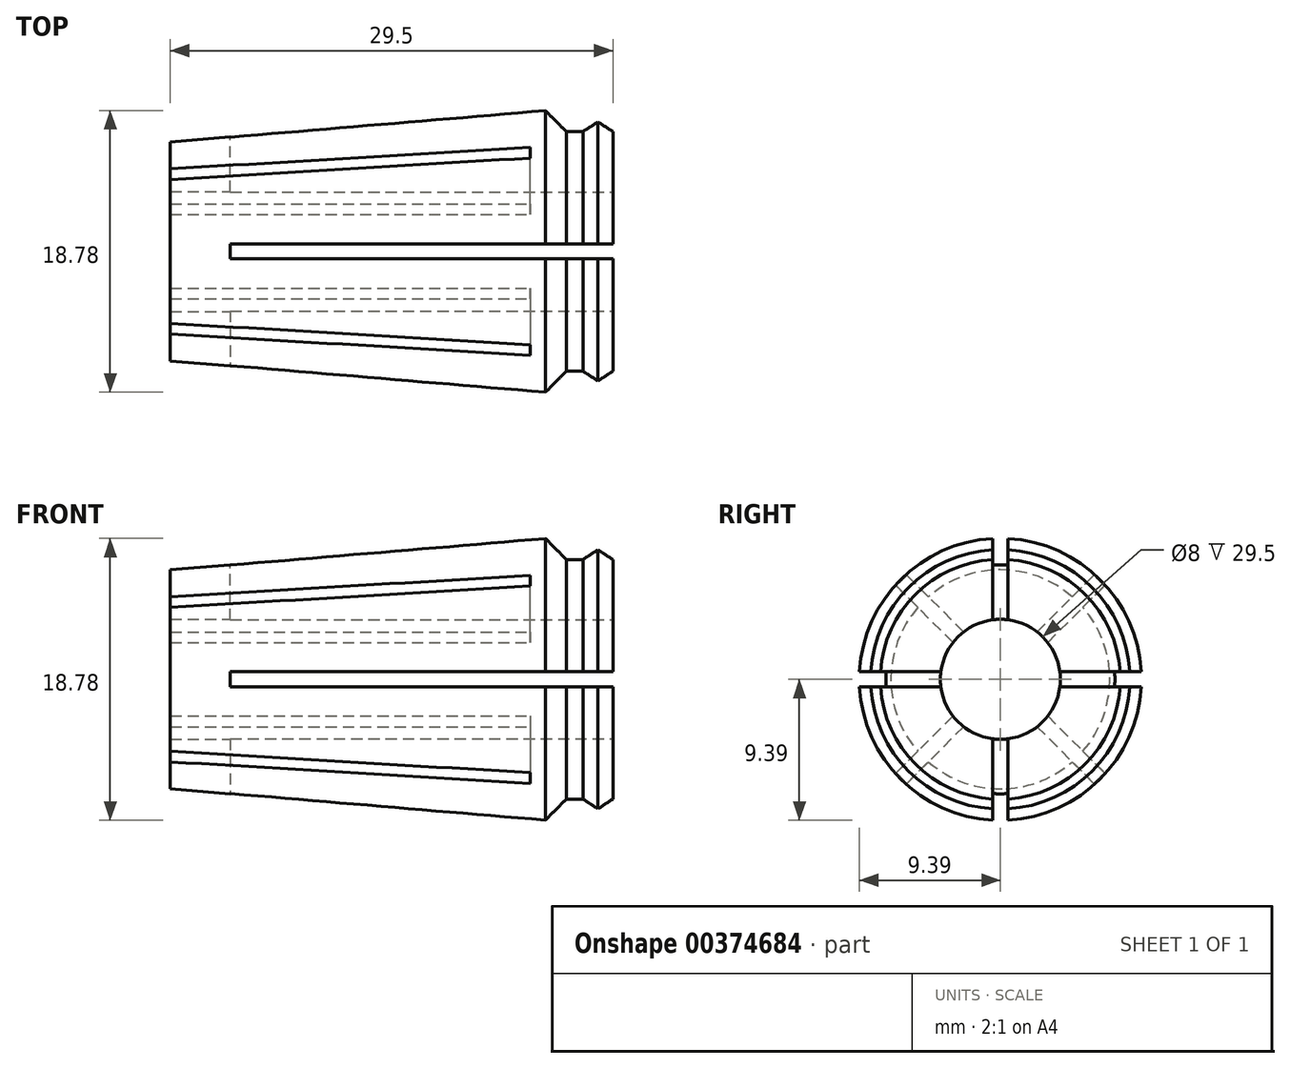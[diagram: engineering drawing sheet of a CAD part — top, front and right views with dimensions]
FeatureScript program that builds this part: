
annotation { "Feature Type Name" : "Feature", "Feature Type Description" : "" }
export const myFeature = defineFeature(function(context is Context, id is Id, definition is map)
    precondition{}
    {
        {
            var Q0;
            Q0=qCreatedBy(makeId("Front.planeOp"),FACE);
            var sketch = newSketch(context, id + "F0", { "sketchPlane" : qUnion([Q0])});
            skLineSegment(sketch, "E0", {"start": v(0, 0) * mm, "end": v(0, 7.3) * mm});
            skLineSegment(sketch, "E1", {"start": v(0, 7.3) * mm, "end": v(25, 9.4) * mm});
            skLineSegment(sketch, "E2", {"start": v(25, 9.4) * mm, "end": v(26.4, 8) * mm});
            skLineSegment(sketch, "E3", {"start": v(26.4, 8) * mm, "end": v(27.5, 8) * mm});
            skLineSegment(sketch, "E4", {"start": v(27.5, 8) * mm, "end": v(28.5, 8.65) * mm});
            skLineSegment(sketch, "E5", {"start": v(28.5, 8.65) * mm, "end": v(29.5, 8) * mm});
            skLineSegment(sketch, "E6", {"start": v(29.5, 8) * mm, "end": v(29.5, 0) * mm});
            skLineSegment(sketch, "E7", {"start": v(0, 0) * mm, "end": v(29.5, 0) * mm});
            skSolve(sketch);
        }
        {
            var Q0;
            Q0=makeQuery(id+"F0.imprint","IMPRINT",FACE,{"disambiguationData":[TD([[makeQuery(id+"F0.imprint","IMPRINT",EDGE,{"derivedFrom":sQuery(id+"F0.wireOp",EDGE,"E0")}),-1.0]])]});
            var Q1;
            Q1=sQuery(id+"F0.wireOp",EDGE,"E7");
            revolve(context, id + "F1", {"entities" : qUnion([Q0]), "axis" : qUnion([Q1]), "revolveType" : RevolveType.FULL});
        }
        {
            var Q0;
            Q0=makeQuery(id+"F1.opRevolve","SWEPT_FACE",FACE,{"disambiguationData":[OSD([sQuery(id+"F0.wireOp",EDGE,"E6")])]});
            var sketch = newSketch(context, id + "F2", { "sketchPlane" : qUnion([Q0])});
            skCircle(sketch, "E8", {"center": v(0, 0) * mm, "radius": 4 * mm});
            skLineSegment(sketch, "E9.0", {"start": v(0.5, 0.5) * mm, "end": v(0.5, 10.05) * mm});
            skLineSegment(sketch, "E10.0", {"start": v(-0.5, 0.5) * mm, "end": v(-0.5, 10.05) * mm});
            skLineSegment(sketch, "E11", {"start": v(-0.5, 10.05) * mm, "end": v(0.5, 10.05) * mm});
            skLineSegment(sketch, "E12.1.0", {"start": v(-0.5, -0.5) * mm, "end": v(-10.05, -0.5) * mm});
            skLineSegment(sketch, "E12.1.1", {"start": v(-0.5, 0.5) * mm, "end": v(-10.05, 0.5) * mm});
            skLineSegment(sketch, "E12.1.2", {"start": v(-10.05, -0.5) * mm, "end": v(-10.05, 0.5) * mm});
            skLineSegment(sketch, "E12.2.0", {"start": v(0.5, -0.5) * mm, "end": v(0.5, -10.05) * mm});
            skLineSegment(sketch, "E12.2.1", {"start": v(-0.5, -0.5) * mm, "end": v(-0.5, -10.05) * mm});
            skLineSegment(sketch, "E12.2.2", {"start": v(0.5, -10.05) * mm, "end": v(-0.5, -10.05) * mm});
            skLineSegment(sketch, "E12.2.3", {"start": v(0, 0) * mm, "end": v(-0.5, 0) * mm});
            skLineSegment(sketch, "E12.3.0", {"start": v(0.5, 0.5) * mm, "end": v(10.05, 0.5) * mm});
            skLineSegment(sketch, "E12.3.1", {"start": v(0.5, -0.5) * mm, "end": v(10.05, -0.5) * mm});
            skLineSegment(sketch, "E12.3.2", {"start": v(10.05, 0.5) * mm, "end": v(10.05, -0.5) * mm});
            skPoint(sketch, "E13.orphan", {"position": v(0.5, 0) * mm});
            skPoint(sketch, "E14.orphan", {"position": v(-0.5, 0) * mm});
            skPoint(sketch, "E15.orphan", {"position": v(0, 0.5) * mm});
            skPoint(sketch, "E16.orphan", {"position": v(0, -0.5) * mm});
            skSolve(sketch);
        }
        {
            var Q0;
            {var subQ0=sQuery(id+"F2.wireOp",EDGE,"E10.0");var subQ1=sQuery(id+"F2.wireOp",EDGE,"E8");var subQ2=makeQuery(id+"F2.imprint","INTERSECT",VERTEX,{"derivedFrom":[subQ1,subQ0]});Q0=makeQuery(id+"F2.imprint","IMPRINT",FACE,{"disambiguationData":[TD([[makeQuery(id+"F2.imprint","IMPRINT",EDGE,{"disambiguationData":[TD([[subQ2,-1.0]])],"derivedFrom":subQ1}),1.0]])]});}
            var Q1;
            {var subQ1=sQuery(id+"F2.wireOp",EDGE,"E8");var subQ5=sQuery(id+"F2.wireOp",EDGE,"E9.0");var subQ6=makeQuery(id+"F2.imprint","INTERSECT",VERTEX,{"derivedFrom":[subQ1,subQ5]});Q1=makeQuery(id+"F2.imprint","IMPRINT",FACE,{"disambiguationData":[TD([[makeQuery(id+"F2.imprint","IMPRINT",EDGE,{"disambiguationData":[TD([[subQ6,-1.0]])],"derivedFrom":subQ1}),1.0]])]});}
            var Q2;
            {var subQ0=sQuery(id+"F2.wireOp",EDGE,"E9.0");var subQ1=sQuery(id+"F2.wireOp",EDGE,"E8");var subQ2=makeQuery(id+"F2.imprint","INTERSECT",VERTEX,{"derivedFrom":[subQ1,subQ0]});Q2=makeQuery(id+"F2.imprint","IMPRINT",FACE,{"disambiguationData":[TD([[makeQuery(id+"F2.imprint","IMPRINT",EDGE,{"disambiguationData":[TD([[subQ2,1.0]])],"derivedFrom":subQ1}),1.0]])]});}
            var Q3;
            {var subQ5=sQuery(id+"F2.wireOp",EDGE,"E12.3.0");var subQ6=sQuery(id+"F2.wireOp",EDGE,"E8");var subQ7=makeQuery(id+"F2.imprint","INTERSECT",VERTEX,{"derivedFrom":[subQ6,subQ5]});Q3=makeQuery(id+"F2.imprint","IMPRINT",FACE,{"disambiguationData":[TD([[makeQuery(id+"F2.imprint","IMPRINT",EDGE,{"disambiguationData":[TD([[subQ7,1.0]])],"derivedFrom":subQ6}),1.0]])]});}
            var Q4;
            {var subQ0=sQuery(id+"F2.wireOp",EDGE,"E12.2.0");var subQ1=sQuery(id+"F2.wireOp",EDGE,"E8");var subQ2=makeQuery(id+"F2.imprint","INTERSECT",VERTEX,{"derivedFrom":[subQ1,subQ0]});Q4=makeQuery(id+"F2.imprint","IMPRINT",FACE,{"disambiguationData":[TD([[makeQuery(id+"F2.imprint","IMPRINT",EDGE,{"disambiguationData":[TD([[subQ2,-1.0]])],"derivedFrom":subQ1}),1.0]])]});}
            var Q5;
            {var subQ0=sQuery(id+"F2.wireOp",EDGE,"E12.2.1");var subQ1=sQuery(id+"F2.wireOp",EDGE,"E8");var subQ2=makeQuery(id+"F2.imprint","INTERSECT",VERTEX,{"derivedFrom":[subQ1,subQ0]});Q5=makeQuery(id+"F2.imprint","IMPRINT",FACE,{"disambiguationData":[TD([[makeQuery(id+"F2.imprint","IMPRINT",EDGE,{"disambiguationData":[TD([[subQ2,-1.0]])],"derivedFrom":subQ1}),1.0]])]});}
            var Q6;
            {var subQ0=sQuery(id+"F2.wireOp",EDGE,"E12.1.0");var subQ1=sQuery(id+"F2.wireOp",EDGE,"E8");var subQ2=makeQuery(id+"F2.imprint","INTERSECT",VERTEX,{"derivedFrom":[subQ1,subQ0]});Q6=makeQuery(id+"F2.imprint","IMPRINT",FACE,{"disambiguationData":[TD([[makeQuery(id+"F2.imprint","IMPRINT",EDGE,{"disambiguationData":[TD([[subQ2,-1.0]])],"derivedFrom":subQ1}),1.0]])]});}
            var Q7;
            {var subQ0=sQuery(id+"F2.wireOp",EDGE,"E12.1.1");var subQ1=sQuery(id+"F2.wireOp",EDGE,"E8");var subQ2=makeQuery(id+"F2.imprint","INTERSECT",VERTEX,{"derivedFrom":[subQ1,subQ0]});Q7=makeQuery(id+"F2.imprint","IMPRINT",FACE,{"disambiguationData":[TD([[makeQuery(id+"F2.imprint","IMPRINT",EDGE,{"disambiguationData":[TD([[subQ2,-1.0]])],"derivedFrom":subQ1}),1.0]])]});}
            var Q8;
            {var subQ1=sQuery(id+"F2.wireOp",EDGE,"E9.0");var subQ3=sQuery(id+"F2.wireOp",EDGE,"E12.3.0");var subQ4=makeQuery(id+"F2.imprint","INTERSECT",VERTEX,{"derivedFrom":[subQ1,subQ3]});Q8=makeQuery(id+"F2.imprint","IMPRINT",FACE,{"disambiguationData":[TD([[makeQuery(id+"F2.imprint","IMPRINT",EDGE,{"disambiguationData":[TD([[subQ4,1.0]])],"derivedFrom":subQ1}),1.0]])]});}
            var Q9;
            {var subQ1=sQuery(id+"F2.wireOp",EDGE,"E10.0");var subQ3=sQuery(id+"F2.wireOp",EDGE,"E12.1.1");var subQ4=makeQuery(id+"F2.imprint","INTERSECT",VERTEX,{"derivedFrom":[subQ1,subQ3]});Q9=makeQuery(id+"F2.imprint","IMPRINT",FACE,{"disambiguationData":[TD([[makeQuery(id+"F2.imprint","IMPRINT",EDGE,{"disambiguationData":[TD([[subQ4,1.0]])],"derivedFrom":subQ1}),-1.0]])]});}
            var Q10;
            {var subQ1=sQuery(id+"F2.wireOp",EDGE,"E12.1.0");var subQ3=sQuery(id+"F2.wireOp",EDGE,"E12.2.1");var subQ4=makeQuery(id+"F2.imprint","INTERSECT",VERTEX,{"derivedFrom":[subQ1,subQ3]});Q10=makeQuery(id+"F2.imprint","IMPRINT",FACE,{"disambiguationData":[TD([[makeQuery(id+"F2.imprint","IMPRINT",EDGE,{"disambiguationData":[TD([[subQ4,1.0]])],"derivedFrom":subQ1}),-1.0]])]});}
            var Q11;
            {var subQ1=sQuery(id+"F2.wireOp",EDGE,"E12.2.0");var subQ3=sQuery(id+"F2.wireOp",EDGE,"E12.3.1");var subQ4=makeQuery(id+"F2.imprint","INTERSECT",VERTEX,{"derivedFrom":[subQ1,subQ3]});Q11=makeQuery(id+"F2.imprint","IMPRINT",FACE,{"disambiguationData":[TD([[makeQuery(id+"F2.imprint","IMPRINT",EDGE,{"disambiguationData":[TD([[subQ4,1.0]])],"derivedFrom":subQ1}),-1.0]])]});}
            extrude(context, id + "F3", {"entities" : qUnion([Q0, Q1, Q2, Q3, Q4, Q5, Q6, Q7, Q8, Q9, Q10, Q11]), "operationType" : NewBodyOperationType.REMOVE, "endBound" : BoundingType.THROUGH_ALL, "oppositeDirection" : true, "depth" : 25 * mm});
        }
        {
            var Q0;
            {var subQ0=sQuery(id+"F2.wireOp",EDGE,"E11");Q0=makeQuery(id+"F2.imprint","IMPRINT",FACE,{"disambiguationData":[TD([[makeQuery(id+"F2.imprint","IMPRINT",EDGE,{"derivedFrom":subQ0}),-1.0]])]});}
            var Q1;
            {var subQ0=sQuery(id+"F2.wireOp",EDGE,"E9.0");var subQ1=sQuery(id+"F2.wireOp",EDGE,"E8");var subQ2=makeQuery(id+"F2.imprint","INTERSECT",VERTEX,{"derivedFrom":[subQ1,subQ0]});Q1=makeQuery(id+"F2.imprint","IMPRINT",FACE,{"disambiguationData":[TD([[makeQuery(id+"F2.imprint","IMPRINT",EDGE,{"disambiguationData":[TD([[subQ2,-1.0]])],"derivedFrom":subQ1}),-1.0]])]});}
            var Q2;
            {var subQ1=sQuery(id+"F2.wireOp",EDGE,"E8");var subQ5=sQuery(id+"F2.wireOp",EDGE,"E9.0");var subQ6=makeQuery(id+"F2.imprint","INTERSECT",VERTEX,{"derivedFrom":[subQ1,subQ5]});Q2=makeQuery(id+"F2.imprint","IMPRINT",FACE,{"disambiguationData":[TD([[makeQuery(id+"F2.imprint","IMPRINT",EDGE,{"disambiguationData":[TD([[subQ6,-1.0]])],"derivedFrom":subQ1}),1.0]])]});}
            var Q3;
            {var subQ0=sQuery(id+"F2.wireOp",EDGE,"E12.2.1");var subQ1=sQuery(id+"F2.wireOp",EDGE,"E8");var subQ2=makeQuery(id+"F2.imprint","INTERSECT",VERTEX,{"derivedFrom":[subQ1,subQ0]});Q3=makeQuery(id+"F2.imprint","IMPRINT",FACE,{"disambiguationData":[TD([[makeQuery(id+"F2.imprint","IMPRINT",EDGE,{"disambiguationData":[TD([[subQ2,-1.0]])],"derivedFrom":subQ1}),1.0]])]});}
            var Q4;
            {var subQ0=sQuery(id+"F2.wireOp",EDGE,"E12.2.1");var subQ1=sQuery(id+"F2.wireOp",EDGE,"E8");var subQ2=makeQuery(id+"F2.imprint","INTERSECT",VERTEX,{"derivedFrom":[subQ1,subQ0]});Q4=makeQuery(id+"F2.imprint","IMPRINT",FACE,{"disambiguationData":[TD([[makeQuery(id+"F2.imprint","IMPRINT",EDGE,{"disambiguationData":[TD([[subQ2,-1.0]])],"derivedFrom":subQ1}),-1.0]])]});}
            var Q5;
            {var subQ0=sQuery(id+"F2.wireOp",EDGE,"E12.2.2");Q5=makeQuery(id+"F2.imprint","IMPRINT",FACE,{"disambiguationData":[TD([[makeQuery(id+"F2.imprint","IMPRINT",EDGE,{"derivedFrom":subQ0}),-1.0]])]});}
            var Q6;
            {var subQ0=sQuery(id+"F2.wireOp",EDGE,"E12.1.1");var subQ1=sQuery(id+"F2.wireOp",EDGE,"E8");var subQ2=makeQuery(id+"F2.imprint","INTERSECT",VERTEX,{"derivedFrom":[subQ1,subQ0]});Q6=makeQuery(id+"F2.imprint","IMPRINT",FACE,{"disambiguationData":[TD([[makeQuery(id+"F2.imprint","IMPRINT",EDGE,{"disambiguationData":[TD([[subQ2,-1.0]])],"derivedFrom":subQ1}),-1.0]])]});}
            var Q7;
            {var subQ0=sQuery(id+"F2.wireOp",EDGE,"E12.1.2");Q7=makeQuery(id+"F2.imprint","IMPRINT",FACE,{"disambiguationData":[TD([[makeQuery(id+"F2.imprint","IMPRINT",EDGE,{"derivedFrom":subQ0}),-1.0]])]});}
            var Q8;
            {var subQ0=sQuery(id+"F2.wireOp",EDGE,"E12.1.1");var subQ1=sQuery(id+"F2.wireOp",EDGE,"E8");var subQ2=makeQuery(id+"F2.imprint","INTERSECT",VERTEX,{"derivedFrom":[subQ1,subQ0]});Q8=makeQuery(id+"F2.imprint","IMPRINT",FACE,{"disambiguationData":[TD([[makeQuery(id+"F2.imprint","IMPRINT",EDGE,{"disambiguationData":[TD([[subQ2,-1.0]])],"derivedFrom":subQ1}),1.0]])]});}
            var Q9;
            {var subQ5=sQuery(id+"F2.wireOp",EDGE,"E12.3.0");var subQ6=sQuery(id+"F2.wireOp",EDGE,"E8");var subQ7=makeQuery(id+"F2.imprint","INTERSECT",VERTEX,{"derivedFrom":[subQ6,subQ5]});Q9=makeQuery(id+"F2.imprint","IMPRINT",FACE,{"disambiguationData":[TD([[makeQuery(id+"F2.imprint","IMPRINT",EDGE,{"disambiguationData":[TD([[subQ7,1.0]])],"derivedFrom":subQ6}),1.0]])]});}
            var Q10;
            {var subQ0=sQuery(id+"F2.wireOp",EDGE,"E12.3.0");var subQ1=sQuery(id+"F2.wireOp",EDGE,"E8");var subQ2=makeQuery(id+"F2.imprint","INTERSECT",VERTEX,{"derivedFrom":[subQ1,subQ0]});Q10=makeQuery(id+"F2.imprint","IMPRINT",FACE,{"disambiguationData":[TD([[makeQuery(id+"F2.imprint","IMPRINT",EDGE,{"disambiguationData":[TD([[subQ2,1.0]])],"derivedFrom":subQ1}),-1.0]])]});}
            var Q11;
            {var subQ0=sQuery(id+"F2.wireOp",EDGE,"E12.3.2");Q11=makeQuery(id+"F2.imprint","IMPRINT",FACE,{"disambiguationData":[TD([[makeQuery(id+"F2.imprint","IMPRINT",EDGE,{"derivedFrom":subQ0}),-1.0]])]});}
            extrude(context, id + "F4", {"entities" : qUnion([Q0, Q1, Q2, Q3, Q4, Q5, Q6, Q7, Q8, Q9, Q10, Q11]), "operationType" : NewBodyOperationType.REMOVE, "oppositeDirection" : true, "depth" : 25.5 * mm});
        }
        {
            var Q0;
            Q0=makeQuery(id+"F1.opRevolve","SWEPT_FACE",FACE,{"disambiguationData":[OSD([sQuery(id+"F0.wireOp",EDGE,"E0")])]});
            var sketch = newSketch(context, id + "F5", { "sketchPlane" : qUnion([Q0])});
            skLineSegment(sketch, "E17.0", {"start": v(0, 0.7) * mm, "end": v(-6.75, 7.46) * mm});
            skLineSegment(sketch, "E18.0", {"start": v(-0.7, 0) * mm, "end": v(-7.46, 6.75) * mm});
            skPoint(sketch, "E19.0", {"position": v(-7.1, 7.1) * mm});
            skLineSegment(sketch, "E20.0", {"start": v(-6.75, 7.46) * mm, "end": v(-7.46, 6.75) * mm});
            skPoint(sketch, "E21.0", {"position": v(-7.46, -6.75) * mm});
            skPoint(sketch, "E22.0", {"position": v(-7.1, -7.1) * mm});
            skLineSegment(sketch, "E23.0", {"start": v(-0.7, 0) * mm, "end": v(-7.46, -6.75) * mm});
            skLineSegment(sketch, "E24.0", {"start": v(0, -0.7) * mm, "end": v(-6.75, -7.46) * mm});
            skLineSegment(sketch, "E25.0", {"start": v(0, 0.7) * mm, "end": v(6.75, 7.46) * mm});
            skLineSegment(sketch, "E26.0", {"start": v(0.7, 0) * mm, "end": v(7.46, 6.75) * mm});
            skLineSegment(sketch, "E27.0", {"start": v(0.7, 0) * mm, "end": v(7.46, -6.75) * mm});
            skLineSegment(sketch, "E28.0", {"start": v(0, -0.7) * mm, "end": v(6.75, -7.46) * mm});
            skPoint(sketch, "E29.0", {"position": v(7.1, -7.1) * mm});
            skLineSegment(sketch, "E30.0", {"start": v(6.75, -7.46) * mm, "end": v(7.46, -6.75) * mm});
            skLineSegment(sketch, "E31.0", {"start": v(7.46, 6.75) * mm, "end": v(6.75, 7.46) * mm});
            skLineSegment(sketch, "E32.0", {"start": v(-7.46, -6.75) * mm, "end": v(-6.75, -7.46) * mm});
            skPoint(sketch, "E33.orphan", {"position": v(0.35, 0.35) * mm});
            skPoint(sketch, "E34.orphan", {"position": v(-0.35, -0.35) * mm});
            skPoint(sketch, "E35.orphan", {"position": v(-0.35, 0.35) * mm});
            skPoint(sketch, "E36.orphan", {"position": v(0.35, -0.35) * mm});
            skSolve(sketch);
        }
        {
            var Q0;
            Q0 = qSketchRegion(id + "F5", true);
            extrude(context, id + "F6", {"entities" : qUnion([Q0]), "operationType" : NewBodyOperationType.REMOVE, "oppositeDirection" : true, "depth" : 24 * mm});
        }
    });
